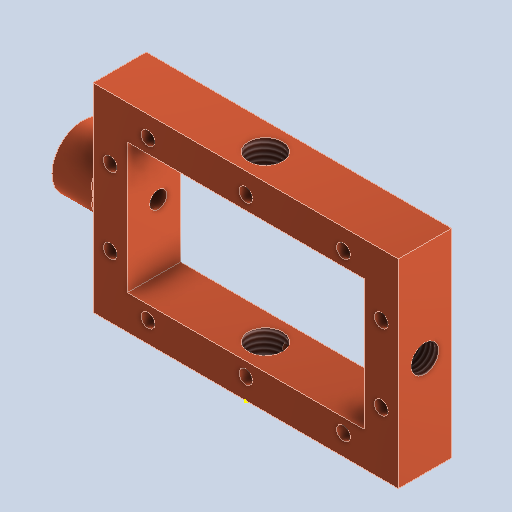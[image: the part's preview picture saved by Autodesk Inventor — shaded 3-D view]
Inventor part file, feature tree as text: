
AUTODESK INVENTOR PART (.ipt)
format: ipt  version: 2025.1 (Build 291241000, 241)  size: 230,912 bytes
history: native  units: mm
features: sketch x9, other x3, plane x2
ambient origin geometry x8: Origin, YZ Plane, XZ Plane, XY Plane, X Axis, Y Axis, Z Axis, Center Point
bodies: Volumenkörper1 (feature_tree)
feature tree (14):
  other  "1152_body.ipt"
  other  "Volumenkörper1::1152_body.ipt"
  other  "TaggingFeature1"
  sketch  "Skizze1"  dims[d0=10.0mm]
  sketch  "Skizze2"
  sketch  "Skizze3"
  sketch  "Skizze4"
  sketch  "Skizze5"
  sketch  "Skizze6"
  sketch  "Skizze7"
  sketch  "Skizze9"
  sketch  "Skizze10"
  plane  "Arbeitsebene1"
  plane  "Arbeitsebene3"
